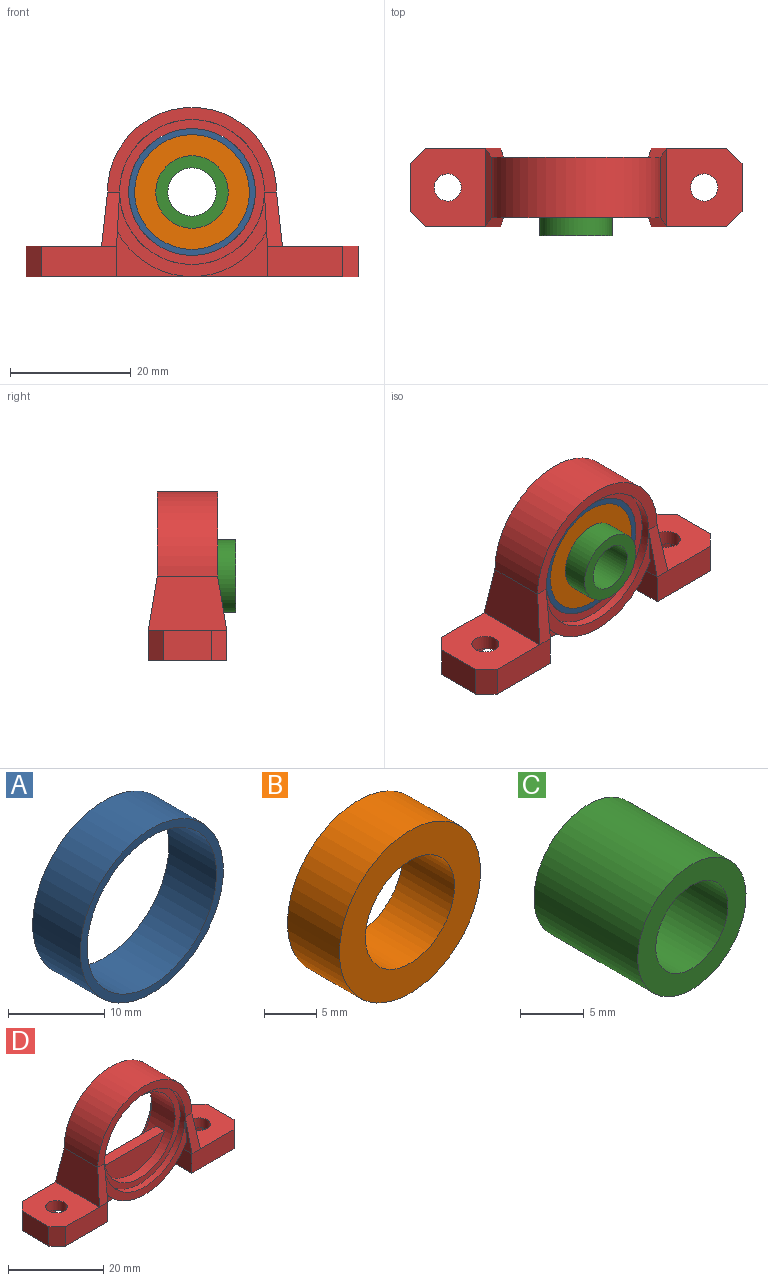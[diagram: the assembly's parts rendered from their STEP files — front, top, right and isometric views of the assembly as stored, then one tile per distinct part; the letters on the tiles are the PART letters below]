
ASSEMBLY  parts=4 mates=6
PART A: 4 faces, bbox 21x7x21 mm
  f0: cylinder r=9.5mm len=19mm, axis (0,1,0), area 417.8mm2, adj f2,f3
  f1: cylinder r=10.5mm len=21mm, axis (0,1,0), area 461.8mm2, adj f2,f3
  f2: plane 21x21mm, normal (0,-1,0), area 62.8mm2, adj f0,f1
  f3: plane 21x21mm, normal (0,1,0), area 62.8mm2, adj f0,f1
PART B: 4 faces, bbox 19x7x19 mm
  f0: cylinder r=6mm len=12mm, axis (0,1,0), area 263.9mm2, adj f2,f3
  f1: cylinder r=9.5mm len=19mm, axis (0,1,0), area 417.8mm2, adj f2,f3
  f2: plane 19x19mm, normal (0,-1,0), area 170.4mm2, adj f0,f1
  f3: plane 19x19mm, normal (0,1,0), area 170.4mm2, adj f0,f1
PART C: 4 faces, bbox 12x11.5x12 mm
  f0: cylinder r=4mm len=11.5mm, axis (0,1,0), area 289mm2, adj f2,f3
  f1: cylinder r=6mm len=12mm, axis (0,1,0), area 433.5mm2, adj f2,f3
  f2: plane 12x12mm, normal (0,-1,0), area 62.8mm2, adj f0,f1
  f3: plane 12x12mm, normal (0,1,0), area 62.8mm2, adj f0,f1
PART D: 62 faces, bbox 55x13x28 mm
  f0: cylinder r=14mm len=24.73mm, axis (0,1,0), area 113.7mm2, adj f2,f13,f44,f50,f55
  f1: cylinder r=14mm len=24.73mm, axis (0,1,0), area 113.7mm2, adj f3,f14,f45,f51,f56
  f2: plane 24.73x14mm, normal (0,1,0), area 64.8mm2, adj f0,f8,f50,f55
  f3: plane 24.73x14mm, normal (0,-1,0), area 64.8mm2, adj f1,f11,f51,f56
  f4: plane 13x12.5mm, normal (0,0,1), area 140.3mm2, adj f22,f23,f24,f25,f27,f54,f61
  f5: cylinder r=14mm len=28mm, axis (0,1,0), area 439.8mm2, adj f9,f10,f54,f58
  f6: cylinder r=10.5mm len=21mm, axis (0,1,0), area 401.5mm2, adj f7,f12,f47,f48,f49
  f7: plane 24x24mm, normal (0,1,0), area 106mm2, adj f6,f8
  f8: cylinder r=12mm len=24mm, axis (0,1,0), area 113.1mm2, adj f2,f7,f9
  f9: plane 28x14mm, normal (0,1,0), area 81.7mm2, adj f5,f8,f52,f59
  f10: plane 28x14mm, normal (0,-1,0), area 81.7mm2, adj f5,f11,f53,f57
  f11: cylinder r=12mm len=24mm, axis (0,1,0), area 113.1mm2, adj f3,f10,f12
  f12: plane 24x24mm, normal (0,-1,0), area 106mm2, adj f6,f11
  f13: plane 12.5x7.43mm, normal (0,1,0), area 27.3mm2, adj f0,f28,f46,f50
  f14: plane 12.5x7.43mm, normal (0,-1,0), area 27.3mm2, adj f1,f26,f46,f51
  f15: plane 10x8mm, normal (0,0,-1), area 63mm2, adj f16,f17,f18,f19,f20,f21,f61
  f16: plane 2.5x1.04mm, normal (0.71,0.71,0), area 3.7mm2, adj f15,f17,f21,f46
  f17: plane 5.93x2.5mm, normal (1,0,0), area 14.8mm2, adj f15,f16,f18,f46
  f18: plane 2.5x1.04mm, normal (0.71,-0.71,0), area 3.7mm2, adj f15,f17,f19,f46
  f19: plane 8.96x2.5mm, normal (0,-1,0), area 22.4mm2, adj f15,f18,f20,f46
  f20: plane 8x2.5mm, normal (-1,0,0), area 20mm2, adj f15,f19,f21,f46
  f21: plane 8.96x2.5mm, normal (0,1,0), area 22.4mm2, adj f15,f16,f20,f46
  f22: plane 5x2.5mm, normal (-0.71,-0.71,0), area 17.7mm2, adj f4,f23,f27,f46
  f23: plane 8x5mm, normal (-1,0,0), area 40mm2, adj f4,f22,f24,f46
  f24: plane 5x2.5mm, normal (-0.71,0.71,0), area 17.7mm2, adj f4,f23,f25,f46
  f25: plane 12.5x5mm, normal (0,1,0), area 62.5mm2, adj f4,f24,f28,f46,f52
  f26: plane 5.25x5mm, normal (1,0,0), area 26.3mm2, adj f14,f27,f46,f51
  f27: plane 12.5x5mm, normal (0,-1,0), area 62.5mm2, adj f4,f22,f26,f46,f53
  f28: plane 5.25x5mm, normal (1,0,0), area 26.3mm2, adj f13,f25,f46,f50
  f29: plane 10x8mm, normal (0,0,-1), area 63mm2, adj f30,f31,f32,f33,f34,f35,f60
  f30: plane 2.5x1.04mm, normal (-0.71,-0.71,0), area 3.7mm2, adj f29,f31,f35,f46
  f31: plane 5.93x2.5mm, normal (-1,0,0), area 14.8mm2, adj f29,f30,f32,f46
  f32: plane 2.5x1.04mm, normal (-0.71,0.71,0), area 3.7mm2, adj f29,f31,f33,f46
  f33: plane 8.96x2.5mm, normal (0,1,0), area 22.4mm2, adj f29,f32,f34,f46
  f34: plane 8x2.5mm, normal (1,0,0), area 20mm2, adj f29,f33,f35,f46
  f35: plane 8.96x2.5mm, normal (0,-1,0), area 22.4mm2, adj f29,f30,f34,f46
  f36: plane 13x12.5mm, normal (0,0,1), area 140.3mm2, adj f37,f38,f39,f40,f42,f58,f60
  f37: plane 5x2.5mm, normal (0.71,0.71,0), area 17.7mm2, adj f36,f38,f42,f46
  f38: plane 8x5mm, normal (1,0,0), area 40mm2, adj f36,f37,f39,f46
  f39: plane 5x2.5mm, normal (0.71,-0.71,0), area 17.7mm2, adj f36,f38,f40,f46
  f40: plane 12.5x5mm, normal (0,-1,0), area 62.5mm2, adj f36,f39,f41,f46,f57
  f41: plane 5.25x5mm, normal (-1,0,0), area 26.3mm2, adj f40,f45,f46,f56
  f42: plane 12.5x5mm, normal (0,1,0), area 62.5mm2, adj f36,f37,f43,f46,f59
  f43: plane 5.25x5mm, normal (-1,0,0), area 26.3mm2, adj f42,f44,f46,f55
  f44: plane 12.5x7.43mm, normal (0,1,0), area 27.3mm2, adj f0,f43,f46,f55
  f45: plane 12.5x7.43mm, normal (0,-1,0), area 27.3mm2, adj f1,f41,f46,f56
  f46: plane 55x13mm, normal (0,0,-1), area 282.1mm2, adj f13,f14,f16,f17,f18,f19,f20,f21
  f47: plane 19.16x2.5mm, normal (0,0,1), area 47.9mm2, adj f6,f48,f49
  f48: plane 19.16x6.2mm, normal (0,-1,0), area 85.5mm2, adj f6,f47
  f49: plane 19.16x6.2mm, normal (0,1,0), area 85.5mm2, adj f6,f47
  f50: plane 9x5.25mm, normal (1,0,-0.06), area 15.9mm2, adj f0,f2,f13,f28,f52
  f51: plane 9x5.25mm, normal (1,0,-0.06), area 15.9mm2, adj f1,f3,f14,f26,f53
  f52: plane 9x3mm, normal (0,0.99,0.16), area 20.5mm2, adj f9,f25,f50,f54
  f53: plane 9x3mm, normal (0,-0.99,0.16), area 20.5mm2, adj f10,f27,f51,f54
  f54: plane 13x9mm, normal (-0.99,0,0.11), area 104.1mm2, adj f4,f5,f52,f53
  f55: plane 9x5.25mm, normal (-1,0,-0.06), area 15.9mm2, adj f0,f2,f43,f44,f59
  f56: plane 9x5.25mm, normal (-1,0,-0.06), area 15.9mm2, adj f1,f3,f41,f45,f57
  f57: plane 9x3mm, normal (0,-0.99,0.16), area 20.5mm2, adj f10,f40,f56,f58
  f58: plane 13x9mm, normal (0.99,0,0.11), area 104.1mm2, adj f5,f36,f57,f59
  f59: plane 9x3mm, normal (0,0.99,0.16), area 20.5mm2, adj f9,f42,f55,f58
  f60: cylinder r=2.25mm len=4.5mm, axis (0,0,1), area 35.3mm2, adj f29,f36
  f61: cylinder r=2.25mm len=4.5mm, axis (0,0,1), area 35.3mm2, adj f4,f15
PLACE A at identity
PLACE B at identity
PLACE C at identity
PLACE D at identity fixed
MATE planar B.f1 <-> C.f1  axis (0,1,0) through (0,0,0)mm
MATE planar A.f1 <-> B.f1  axis (0,1,0) through (0,0,0)mm
MATE planar D.f0 <-> A.f1  axis (0,1,0) through (0,0,0)mm
MATE slider D.f0 <-> A.f1  axis (0,1,0) through (0,-3.5,0)mm
MATE slider C.f0 <-> B.f0  axis (0,1,0) through (0,0,0)mm
MATE slider C.f0 <-> A.f0  axis (0,1,0) through (0,0,0)mm
